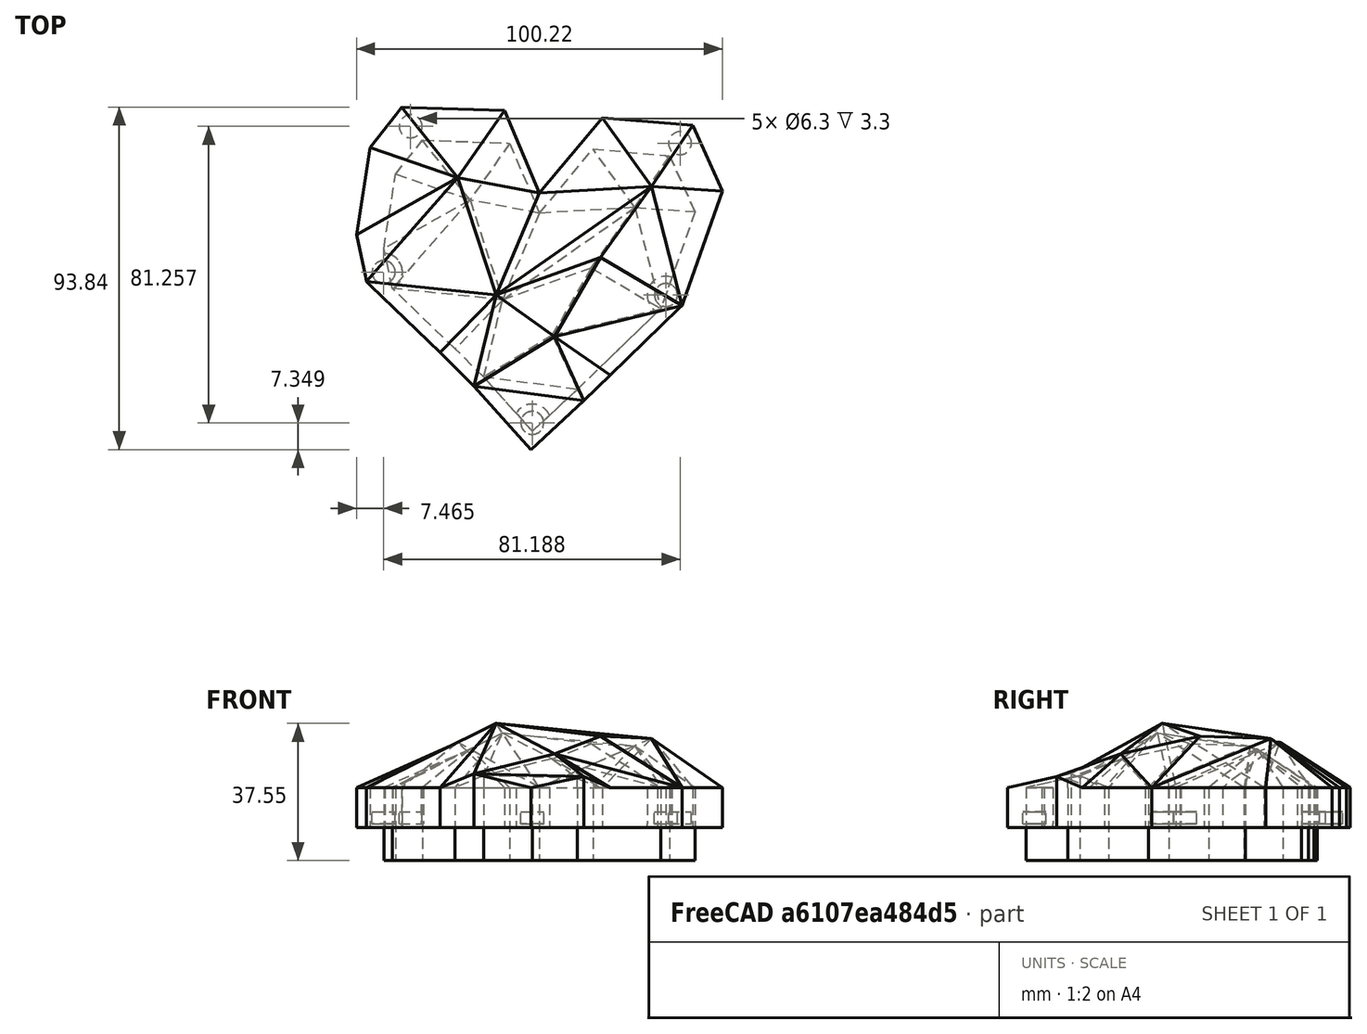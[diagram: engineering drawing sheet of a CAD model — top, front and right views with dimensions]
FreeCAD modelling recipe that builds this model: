
FCSTD DOCUMENT  (FreeCAD 0.20RUnknown)
Label: heart2
License: All rights reserved
LicenseURL: http://en.wikipedia.org/wiki/All_rights_reserved
objects: Part::Feature×4, Sketcher::SketchObject×4, PartDesign::Pad×4, Mesh::Feature×2, PartDesign::FeatureBase×2, PartDesign::Body×2, PartDesign::Boolean×1, PartDesign::Hole×1
note: 23 computed .brp shape members not serialized (recipe doc carries the construction recipe); baked Part::Feature solids carry a one-line shape summary decoded from their .brp

FEATURE [Mesh::Feature] heart_poly_solid
FEATURE [Part::Feature] heart_poly_solid001
  shape: bbox 100.2 x 93.84 x 17.55 mm, 41 faces, 0 solids (baked)
FEATURE [Part::Feature] heart_poly_solid001_solid  label="heart_poly_solid001 (Solid)"
  shape: bbox 100.2 x 93.84 x 17.55 mm, 41 faces (baked)
FEATURE [PartDesign::FeatureBase] BaseFeature
  BaseFeature = -> heart_poly_solid001_solid
FEATURE [Mesh::Feature] heart_poly_solid002
  Placement = pos=(0,-2,0) rot=(0,0,1;0rad)
FEATURE [Part::Feature] heart_poly_solid002001
  shape: bbox 85.18 x 79.76 x 14.92 mm, 41 faces, 0 solids (baked)
FEATURE [Part::Feature] heart_poly_solid002001_solid  label="heart_poly_solid002001 (Solid)"
  shape: bbox 85.18 x 79.76 x 14.92 mm, 41 faces (baked)
FEATURE [PartDesign::FeatureBase] BaseFeature001
  BaseFeature = -> heart_poly_solid002001_solid
FEATURE [Sketcher::SketchObject] Sketch
  ExternalGeometry = -> [BaseFeature001]
  FullyConstrained = true
  MapMode = 5
  Support = -> [XY_Plane001]
  sketch-geometry (15):
    g0: LineSegment StartX=-0.00387275 StartY=17.8517 StartZ=0 EndX=14.6361 EndY=35.4352 EndZ=0
    g1: LineSegment StartX=14.6361 StartY=35.4352 StartZ=0 EndX=35.6665 EndY=33.6149 EndZ=0
    g2: LineSegment StartX=35.6665 StartY=33.6149 StartZ=0 EndX=42.5605 EndY=18.2778 EndZ=0
    g3: LineSegment StartX=42.5605 StartY=18.2778 StartZ=0 EndX=33.2374 EndY=-8.29477 EndZ=0
    g4: LineSegment StartX=33.2374 StartY=-8.29477 StartZ=0 EndX=16.4507 EndY=-24.4834 EndZ=0
    g5: LineSegment StartX=16.4507 StartY=-24.4834 StartZ=0 EndX=10.3474 EndY=-30.4149 EndZ=0
    g6: LineSegment StartX=10.3474 StartY=-30.4149 StartZ=0 EndX=-1.95112 EndY=-41.8865 EndZ=0
    g7: LineSegment StartX=-1.95112 StartY=-41.8865 StartZ=0 EndX=-15.276 EndY=-27.0624 EndZ=0
    g8: LineSegment StartX=-15.276 StartY=-27.0624 StartZ=0 EndX=-23.133 EndY=-19.2867 EndZ=0
    g9: LineSegment StartX=-23.133 StartY=-19.2867 StartZ=0 EndX=-40.2825 EndY=-2.75831 EndZ=0
    g10: LineSegment StartX=-40.2825 StartY=-2.75831 StartZ=0 EndX=-42.6242 EndY=8.17997 EndZ=0
    g11: LineSegment StartX=-42.6242 StartY=8.17997 StartZ=0 EndX=-39.4286 EndY=28.5136 EndZ=0
    g12: LineSegment StartX=-39.4286 StartY=28.5136 StartZ=0 EndX=-32.0751 EndY=37.8747 EndZ=0
    g13: LineSegment StartX=-32.0751 StartY=37.8747 StartZ=0 EndX=-8.17592 EndY=37.0619 EndZ=0
    g14: LineSegment StartX=-8.17592 StartY=37.0619 StartZ=0 EndX=-0.00387275 EndY=17.8517 EndZ=0
  constraints (30):
    c: Coincident(g-5,g0)
    c: Coincident(g0,g-6)
    c: Coincident(g0,g1)
    c: Coincident(g1,g-7)
    c: Coincident(g1,g2)
    c: Coincident(g2,g-8)
    c: Coincident(g2,g3)
    c: Coincident(g3,g-9)
    c: Coincident(g3,g4)
    c: Coincident(g4,g-10)
    c: Coincident(g4,g5)
    c: Coincident(g5,g-11)
    c: Coincident(g5,g6)
    c: Coincident(g6,g-12)
    c: Coincident(g6,g7)
    c: Coincident(g7,g-13)
    c: Coincident(g7,g8)
    c: Coincident(g8,g-14)
    c: Coincident(g8,g9)
    c: Coincident(g9,g-15)
    c: Coincident(g9,g10)
    c: Coincident(g10,g-16)
    c: Coincident(g10,g11)
    c: Coincident(g11,g-17)
    c: Coincident(g11,g12)
    c: Coincident(g12,g-17)
    c: Coincident(g12,g13)
    c: Coincident(g13,g-4)
    c: Coincident(g13,g14)
    c: Coincident(g14,g0)
FEATURE [PartDesign::Pad] Pad
  BaseFeature = -> BaseFeature001
  Direction = (0,0,1)
  Length = 20
  Length2 = 10
  Profile = -> Sketch
  ReferenceAxis = -> Sketch [N_Axis]
  Reversed = true
  Type = 0
FEATURE [PartDesign::Body] Body001
  BaseFeature = -> heart_poly_solid002001_solid
  Group = -> [BaseFeature001,Sketch,Pad]
  Origin = -> Origin001
  Tip = -> Pad
FEATURE [Sketcher::SketchObject] Sketch001
  ExternalGeometry = -> [BaseFeature]
  FullyConstrained = true
  MapMode = 5
  Support = -> [XY_Plane]
  sketch-geometry (15):
    g0: LineSegment StartX=-2.29544 StartY=-46.9253 StartZ=0 EndX=12.1734 EndY=-33.4294 EndZ=0
    g1: LineSegment StartX=12.1734 StartY=-33.4294 StartZ=0 EndX=19.3538 EndY=-26.4511 EndZ=0
    g2: LineSegment StartX=19.3538 StartY=-26.4511 StartZ=0 EndX=39.1029 EndY=-7.40561 EndZ=0
    g3: LineSegment StartX=39.1029 StartY=-7.40561 StartZ=0 EndX=50.0711 EndY=23.8562 EndZ=0
    g4: LineSegment StartX=50.0711 StartY=23.8562 StartZ=0 EndX=41.9606 EndY=41.8999 EndZ=0
    g5: LineSegment StartX=41.9606 StartY=41.8999 StartZ=0 EndX=17.2189 EndY=44.0414 EndZ=0
    g6: LineSegment StartX=17.2189 StartY=44.0414 StartZ=0 EndX=-0.00455618 EndY=23.355 EndZ=0
    g7: LineSegment StartX=-0.00455618 StartY=23.355 StartZ=0 EndX=-9.61873 EndY=45.9551 EndZ=0
    g8: LineSegment StartX=-9.61873 StartY=45.9551 StartZ=0 EndX=-37.7354 EndY=46.9115 EndZ=0
    g9: LineSegment StartX=-37.7354 StartY=46.9115 StartZ=0 EndX=-46.3866 EndY=35.8983 EndZ=0
    g10: LineSegment StartX=-46.3866 StartY=35.8983 StartZ=0 EndX=-50.1462 EndY=11.9764 EndZ=0
    g11: LineSegment StartX=-50.1462 StartY=11.9764 StartZ=0 EndX=-47.3912 EndY=-0.892128 EndZ=0
    g12: LineSegment StartX=-47.3912 StartY=-0.892128 StartZ=0 EndX=-27.2153 EndY=-20.3373 EndZ=0
    g13: LineSegment StartX=-27.2153 StartY=-20.3373 StartZ=0 EndX=-17.9718 EndY=-29.4852 EndZ=0
    g14: LineSegment StartX=-17.9718 StartY=-29.4852 StartZ=0 EndX=-2.29544 EndY=-46.9253 EndZ=0
  constraints (30):
    c: Coincident(g-11,g0)
    c: Coincident(g0,g-11)
    c: Coincident(g0,g1)
    c: Coincident(g1,g-10)
    c: Coincident(g1,g2)
    c: Coincident(g2,g-9)
    c: Coincident(g2,g3)
    c: Coincident(g3,g-8)
    c: Coincident(g3,g4)
    c: Coincident(g4,g-7)
    c: Coincident(g4,g5)
    c: Coincident(g5,g-6)
    c: Coincident(g5,g6)
    c: Coincident(g6,g-5)
    c: Coincident(g6,g7)
    c: Coincident(g7,g-4)
    c: Coincident(g7,g8)
    c: Coincident(g8,g-16)
    c: Coincident(g8,g9)
    c: Coincident(g9,g-16)
    c: Coincident(g9,g10)
    c: Coincident(g10,g-15)
    c: Coincident(g10,g11)
    c: Coincident(g11,g-14)
    c: Coincident(g11,g12)
    c: Coincident(g12,g-13)
    c: Coincident(g12,g13)
    c: Coincident(g13,g-12)
    c: Coincident(g13,g14)
    c: Coincident(g14,g0)
FEATURE [PartDesign::Pad] Pad001
  BaseFeature = -> BaseFeature
  Direction = (0,0,1)
  Length = 10
  Length2 = 10
  Profile = -> Sketch001
  ReferenceAxis = -> Sketch001 [N_Axis]
  Reversed = true
  Type = 0
FEATURE [PartDesign::Boolean] Boolean
  BaseFeature = -> Pad001
  Group = -> [heart_poly_solid002001_solid,Body001]
  Type = 1
FEATURE [Sketcher::SketchObject] Sketch002
  ExternalGeometry = -> [Boolean]
  FullyConstrained = true
  MapMode = 5
  Placement = pos=(0,0,-10) rot=(1,0,0;3.14159rad)
  Support = -> [Boolean]
  expr: Constraints[0] = 6 + 2 * 0.15
  sketch-geometry (8):
    g0: Circle CenterX=-35.2994 CenterY=-41.6756 CenterZ=0 NormalX=0 NormalY=0 NormalZ=1 AngleXU=0 Radius=3.15
    g1: Circle CenterX=-35.2994 CenterY=-41.6756 CenterZ=0 NormalX=0 NormalY=0 NormalZ=1 AngleXU=0 Radius=5.15
    g2: LineSegment StartX=-35.2994 StartY=-44.8256 StartZ=0 EndX=-35.2994 EndY=-46.8256 EndZ=0
    g3: LineSegment StartX=-35.2994 StartY=-41.6756 StartZ=0 EndX=-35.2994 EndY=-44.8256 EndZ=0
    g4: Circle CenterX=38.5033 CenterY=-37.0299 CenterZ=0 NormalX=0 NormalY=0 NormalZ=1 AngleXU=0 Radius=5.15
    g5: Circle CenterX=-1.97215 CenterY=39.5811 CenterZ=0 NormalX=0 NormalY=0 NormalZ=1 AngleXU=0 Radius=5.15
    g6: Circle CenterX=-42.6846 CenterY=-1.7243 CenterZ=0 NormalX=0 NormalY=0 NormalZ=1 AngleXU=0 Radius=5.15
    g7: Circle CenterX=34.648 CenterY=4.54714 CenterZ=0 NormalX=0 NormalY=0 NormalZ=1 AngleXU=0 Radius=5.15
  constraints (23):
    c: Diameter(g0) = 6.3
    c: Coincident(g1,g0)
    c: PointOnObject(g2,g0)
    c: PointOnObject(g2,g1)
    c: Vertical(g2)
    c: DistanceY(g2,g2) = 2
    c: Coincident(g3,g0)
    c: Coincident(g3,g2)
    c: Vertical(g3)
    c: Tangent(g1,g-4)
    c: Tangent(g1,g-3)
    c: Equal(g1,g4)
    c: Tangent(g4,g-5)
    c: Tangent(g4,g-6)
    c: Equal(g1,g5)
    c: Tangent(g5,g-11)
    c: Tangent(g5,g-12)
    c: Equal(g1,g6)
    c: Equal(g1,g7)
    c: Tangent(g6,g-9)
    c: Tangent(g6,g-10)
    c: Tangent(g7,g-7)
    c: Tangent(g7,g-8)
FEATURE [PartDesign::Pad] Pad002
  BaseFeature = -> Boolean
  Direction = (0,0,-1)
  Length = 10
  Length2 = 10
  Profile = -> Sketch002
  ReferenceAxis = -> Sketch002 [N_Axis]
  Reversed = true
  Type = 0
FEATURE [PartDesign::Hole] Hole
  BaseFeature = -> Pad002
  CustomThreadClearance = 0
  Depth = 3.3
  DepthType = 0
  Diameter = 6.3
  DrillForDepth = false
  DrillPoint = 0
  DrillPointAngle = 118
  HoleCutCountersinkAngle = 90
  HoleCutCustomValues = false
  HoleCutDepth = 5.67
  HoleCutDiameter = 10.08
  HoleCutType = 0
  ModelThread = false
  Profile = -> Sketch002
  Tapered = false
  TaperedAngle = 90
  ThreadClass = 0
  ThreadDepth = 3.3
  ThreadDepthType = 0
  ThreadDirection = 0
  ThreadFit = 0
  ThreadSize = 0
  ThreadType = 0
  Threaded = false
  UseCustomThreadClearance = false
  expr: Depth = 3 + 2 * 0.15
  expr: Diameter = 6 + 2 * 0.15
FEATURE [Sketcher::SketchObject] Sketch003
  ExternalGeometry = -> [Hole]
  FullyConstrained = true
  MapMode = 5
  Placement = pos=(0,0,-10) rot=(1,0,0;3.14159rad)
  Support = -> [Hole]
  sketch-geometry (34):
    g0: LineSegment StartX=-2.29544 StartY=46.9253 StartZ=0 EndX=12.1734 EndY=33.4294 EndZ=0
    g1: LineSegment StartX=12.1734 StartY=33.4294 StartZ=0 EndX=19.3538 EndY=26.4511 EndZ=0
    g2: LineSegment StartX=19.3538 StartY=26.4511 StartZ=0 EndX=39.1029 EndY=7.40561 EndZ=0
    g3: LineSegment StartX=39.1029 StartY=7.40561 StartZ=0 EndX=50.0711 EndY=-23.8562 EndZ=0
    g4: LineSegment StartX=50.0711 StartY=-23.8562 StartZ=0 EndX=41.9606 EndY=-41.8999 EndZ=0
    g5: LineSegment StartX=41.9606 StartY=-41.8999 StartZ=0 EndX=17.2189 EndY=-44.0414 EndZ=0
    g6: LineSegment StartX=17.2189 StartY=-44.0414 StartZ=0 EndX=-0.00455618 EndY=-23.355 EndZ=0
    g7: LineSegment StartX=-0.00455618 StartY=-23.355 StartZ=0 EndX=-9.61873 EndY=-45.9551 EndZ=0
    g8: LineSegment StartX=-9.61873 StartY=-45.9551 StartZ=0 EndX=-37.7354 EndY=-46.9115 EndZ=0
    g9: LineSegment StartX=-37.7354 StartY=-46.9115 StartZ=0 EndX=-46.3866 EndY=-35.8983 EndZ=0
    g10: LineSegment StartX=-46.3866 StartY=-35.8983 StartZ=0 EndX=-50.1462 EndY=-11.9764 EndZ=0
    g11: LineSegment StartX=-50.1462 StartY=-11.9764 StartZ=0 EndX=-47.3912 EndY=0.892128 EndZ=0
    g12: LineSegment StartX=-47.3912 StartY=0.892128 StartZ=0 EndX=-27.2153 EndY=20.3373 EndZ=0
    g13: LineSegment StartX=-27.2153 StartY=20.3373 StartZ=0 EndX=-17.9718 EndY=29.4852 EndZ=0
    g14: LineSegment StartX=-17.9718 StartY=29.4852 StartZ=0 EndX=-2.29544 EndY=46.9253 EndZ=0
    g15: LineSegment StartX=-6.39495 StartY=36.9427 StartZ=0 EndX=-15.276 EndY=27.0624 EndZ=0
    g16: LineSegment StartX=-15.276 StartY=27.0624 StartZ=0 EndX=-23.133 EndY=19.2867 EndZ=0
    g17: LineSegment StartX=-23.133 StartY=19.2867 StartZ=0 EndX=-40.2338 EndY=2.80519 EndZ=0
    g18: LineSegment StartX=-42.3423 StartY=-6.86291 StartZ=0 EndX=-42.6242 EndY=-8.17997 EndZ=0
    g19: LineSegment StartX=-42.6242 StartY=-8.17997 StartZ=0 EndX=-39.4286 EndY=-28.5136 EndZ=0
    g20: LineSegment StartX=-39.4286 StartY=-28.5136 StartZ=0 EndX=-32.0751 EndY=-37.8747 EndZ=0
    g21: LineSegment StartX=-32.0751 StartY=-37.8747 StartZ=0 EndX=-8.17592 EndY=-37.0619 EndZ=0
    g22: LineSegment StartX=-8.17592 StartY=-37.0619 StartZ=0 EndX=-0.00387275 EndY=-17.8517 EndZ=0
    g23: LineSegment StartX=-0.00387275 StartY=-17.8517 StartZ=0 EndX=14.6361 EndY=-35.4352 EndZ=0
    g24: LineSegment StartX=14.6361 StartY=-35.4352 StartZ=0 EndX=34.5661 EndY=-33.7101 EndZ=0
    g25: LineSegment StartX=42.5605 StartY=-18.2778 StartZ=0 EndX=36.2675 EndY=-0.34159 EndZ=0
    g26: LineSegment StartX=2.74239 StartY=37.5086 StartZ=0 EndX=10.3474 EndY=30.4149 EndZ=0
    g27: LineSegment StartX=10.3474 StartY=30.4149 StartZ=0 EndX=16.4507 EndY=24.4834 EndZ=0
    g28: LineSegment StartX=16.4507 StartY=24.4834 StartZ=0 EndX=32.3463 EndY=9.15416 EndZ=0
    g29: ArcOfCircle CenterX=-1.97215 CenterY=39.5811 CenterZ=0 NormalX=0 NormalY=0 NormalZ=1 AngleXU=0 Radius=5.15 StartAngle=3.67947 EndAngle=5.869
    g30: ArcOfCircle CenterX=34.648 CenterY=4.54714 CenterZ=0 NormalX=0 NormalY=0 NormalZ=1 AngleXU=0 Radius=5.15 StartAngle=2.03413 EndAngle=5.03229
    g31: ArcOfCircle CenterX=-42.6846 CenterY=-1.7243 CenterZ=0 NormalX=0 NormalY=0 NormalZ=1 AngleXU=0 Radius=5.15 StartAngle=4.77891 EndAngle=7.35802
    g32: LineSegment StartX=42.5605 StartY=-18.2778 StartZ=0 EndX=36.2026 EndY=-32.4224 EndZ=0
    g33: ArcOfCircle CenterX=38.5033 CenterY=-37.0299 CenterZ=0 NormalX=0 NormalY=0 NormalZ=1 AngleXU=0 Radius=5.15 StartAngle=2.03392 EndAngle=2.44108
  constraints (72):
    c: Coincident(g-49,g0)
    c: Coincident(g0,g-9)
    c: Coincident(g0,g1)
    c: Coincident(g1,g-10)
    c: Coincident(g1,g2)
    c: Coincident(g2,g-12)
    c: Coincident(g2,g3)
    c: Coincident(g3,g-16)
    c: Coincident(g3,g4)
    c: Coincident(g4,g-18)
    c: Coincident(g4,g5)
    c: Coincident(g5,g-20)
    c: Coincident(g5,g6)
    c: Coincident(g6,g-25)
    c: Coincident(g6,g7)
    c: Coincident(g7,g-27)
    c: Coincident(g7,g8)
    c: Coincident(g8,g-29)
    c: Coincident(g8,g9)
    c: Coincident(g9,g-34)
    c: Coincident(g9,g10)
    c: Coincident(g10,g-36)
    c: Coincident(g10,g11)
    c: Coincident(g11,g-39)
    c: Coincident(g11,g12)
    c: Coincident(g12,g-48)
    c: Coincident(g12,g13)
    c: Coincident(g13,g-48)
    c: Coincident(g13,g14)
    c: Coincident(g14,g0)
    c: Coincident(g-46,g15)
    c: Coincident(g15,g-46)
    c: Coincident(g15,g16)
    c: Coincident(g16,g-45)
    c: Coincident(g16,g17)
    c: Coincident(g17,g-42)
    c: Coincident(g-44,g18)
    c: Coincident(g18,g-44)
    c: Coincident(g18,g19)
    c: Coincident(g19,g-35)
    c: Coincident(g19,g20)
    c: Coincident(g20,g-32)
    c: Coincident(g20,g21)
    c: Coincident(g21,g-30)
    c: Coincident(g21,g22)
    c: Coincident(g22,g-26)
    c: Coincident(g22,g23)
    c: Coincident(g23,g-24)
    c: Coincident(g23,g24)
    c: Coincident(g24,g-22)
    c: Coincident(g25,g-15)
    c: Coincident(g-6,g26)
    c: Coincident(g26,g-8)
    c: Coincident(g26,g27)
    c: Coincident(g27,g-8)
    c: Coincident(g27,g28)
    c: Coincident(g28,g-13)
    c: Coincident(g29,g-5)
    c: Coincident(g29,g15)
    c: Coincident(g29,g26)
    c: Coincident(g30,g-13)
    c: Coincident(g30,g28)
    c: Coincident(g30,g25)
    c: Coincident(g31,g-43)
    c: Coincident(g31,g17)
    c: Coincident(g31,g18)
    c: Coincident(g32,g25)
    c: Coincident(g25,g-23)
    c: Coincident(g32,g-23)
    c: Coincident(g33,g-22)
    c: Coincident(g33,g24)
    c: Coincident(g33,g32)
FEATURE [PartDesign::Pad] Pad003
  BaseFeature = -> Hole
  Direction = (0,0,-1)
  Length = 1
  Length2 = 10
  Profile = -> Sketch003
  ReferenceAxis = -> Sketch003 [N_Axis]
  Type = 0
FEATURE [PartDesign::Body] Body
  BaseFeature = -> heart_poly_solid001_solid
  Group = -> [BaseFeature,Sketch001,Pad001,Boolean,Sketch002,Pad002,Hole,Sketch003,Pad003]
  Origin = -> Origin
  Tip = -> Pad003
